# Revit family: RN 80033 Optipress-Aquaplus-Übergang
name_source: partatom
category: Rohrformteile
units: mm (PartAtom-declared; Revit-internal decimal feet)

## family parameters
Arbeitsebenenbasiert = Nein
Beim Laden mit Abzugskörper schneiden = Nein
Bemaßung runder Anschluss = Durchmesser verwenden
Gemeinsam genutzt = Nein
Immer vertikal = Ja
Teiletyp = Verbindung

## types (20) — shared parameters
1.010.00.2 Blattnummer der Richtlinie = 29
1.010.00.3 Ausgabedatum (Monat) der Richtlinie = 201308
1.010.00.4 Herstellername = R. Nussbaum AG
1.010.00.5 Revisionsdatum der Datei = 20190521
1.010.00.6 Webadresse des Herstellers = http://www.nussbaum.ch
1.100.00.4 Produktbezeichnung = Versorgung
1.110.00.2 Index = 4
1.110.00.4 Produktbezeichnung = Optipress
1.960/3L.00.8 Link (URL) = https://www.nussbaum.ch
29.700.00.4 Produktname = Optipress-Aquaplus-Übergang, mit Innengewinde
29.700.00.5 Produktkennung = 2
29.700.00.6 Querschnittsform = 1
29.700.00.7 Nennweitensystem = DN
29.700.00.8 Nenndrucksystem = PN
29.710.02.4 Nenndruck = 16
29.710.02.5 max. zul. Überdruck [hPa] = 1600
29.710.02.7 max. zul. Dauer-Betriebsdruck [hPa] = 1600
29.710.02.9 max. zul. Dauer-Betriebstemperatur [°C] = 95
Connector Visibility = Nein
EnclosingSpace Visibility = Nein

## per-type parameters (varying)
- 80033.22, Optipress-Aquaplus-Übergang, mit Innengewinde, DN=12x15, L=49, Rp=½: 1.800.00.3 TGA-Nummer=01900400000000000000000000000000000000000000000022000000000000000001; 1.810.00.3 Hersteller-Bestellnummer=80033.22; 1.810.00.4 DATANORM-Nummer=80033.22; 1.810.00.5 StLB-Nummer=267.132; 1.810.00.6 GTIN-Nummer=7612945051370; 29.710.02.10 Formstück-Gewicht [kg]=0.044; 29.710.02.3 Benennung=Optipress-Aquaplus-Übergang, mit Innengewinde, DN=12x15, L=49, Rp=½; CONNECTOR0_DIAMETER_dX_0r=12 mm  [stored 0.0393701 ft]; CONNECTOR0_dX_01=22 mm; CONNECTOR0_ref_dX=22 mm; CONNECTOR1_DIAMETER_dX_0r=15 mm  [stored 0.0492126 ft]; CONNECTOR1_dX_00=36 mm  [stored 0.11811 ft]; CONNECTOR1_dX_01=49 mm; CONNECTOR1_ref_dX=36 mm  [stored 0.11811 ft]; R. Nussbaum AG 80033.22 de Visibility=Ja; R. Nussbaum AG 80033.23 de Visibility=Nein; R. Nussbaum AG 80033.24 de Visibility=Nein; R. Nussbaum AG 80033.25 de Visibility=Nein; R. Nussbaum AG 80033.26 de Visibility=Nein; R. Nussbaum AG 80033.27 de Visibility=Nein; R. Nussbaum AG 80033.28 de Visibility=Nein; R. Nussbaum AG 80033.29 de Visibility=Nein; R. Nussbaum AG 80033.30 de Visibility=Nein; R. Nussbaum AG 80033.31 de Visibility=Nein; R. Nussbaum AG 80033.32 de Visibility=Nein; R. Nussbaum AG 80033.33 de Visibility=Nein; R. Nussbaum AG 80033.34 de Visibility=Nein; R. Nussbaum AG 80033.35 de Visibility=Nein; R. Nussbaum AG 80033.36 de Visibility=Nein; R. Nussbaum AG 80033.37 de Visibility=Nein; R. Nussbaum AG 80033.38 de Visibility=Nein; R. Nussbaum AG 80033.70 de Visibility=Nein; R. Nussbaum AG 80033.71 de Visibility=Nein; R. Nussbaum AG 80033.72 de Visibility=Nein
- 80033.23, Optipress-Aquaplus-Übergang, mit Innengewinde, DN=15, L=48, Rp=½: 1.800.00.3 TGA-Nummer=01900400000000000000000000000000000000000000000022000000000000000002; 1.810.00.3 Hersteller-Bestellnummer=80033.23; 1.810.00.4 DATANORM-Nummer=80033.23; 1.810.00.5 StLB-Nummer=267.133; 1.810.00.6 GTIN-Nummer=7612945051462; 29.710.02.10 Formstück-Gewicht [kg]=0.047; 29.710.02.3 Benennung=Optipress-Aquaplus-Übergang, mit Innengewinde, DN=15, L=48, Rp=½; CONNECTOR0_DIAMETER_dX_0r=15 mm  [stored 0.0492126 ft]; CONNECTOR0_dX_01=22 mm; CONNECTOR0_ref_dX=22 mm; CONNECTOR1_DIAMETER_dX_0r=15 mm  [stored 0.0492126 ft]; CONNECTOR1_dX_00=35 mm; CONNECTOR1_dX_01=48 mm; CONNECTOR1_ref_dX=35 mm; R. Nussbaum AG 80033.22 de Visibility=Nein; R. Nussbaum AG 80033.23 de Visibility=Ja; R. Nussbaum AG 80033.24 de Visibility=Nein; R. Nussbaum AG 80033.25 de Visibility=Nein; R. Nussbaum AG 80033.26 de Visibility=Nein; R. Nussbaum AG 80033.27 de Visibility=Nein; R. Nussbaum AG 80033.28 de Visibility=Nein; R. Nussbaum AG 80033.29 de Visibility=Nein; R. Nussbaum AG 80033.30 de Visibility=Nein; R. Nussbaum AG 80033.31 de Visibility=Nein; R. Nussbaum AG 80033.32 de Visibility=Nein; R. Nussbaum AG 80033.33 de Visibility=Nein; R. Nussbaum AG 80033.34 de Visibility=Nein; R. Nussbaum AG 80033.35 de Visibility=Nein; R. Nussbaum AG 80033.36 de Visibility=Nein; R. Nussbaum AG 80033.37 de Visibility=Nein; R. Nussbaum AG 80033.38 de Visibility=Nein; R. Nussbaum AG 80033.70 de Visibility=Nein; R. Nussbaum AG 80033.71 de Visibility=Nein; R. Nussbaum AG 80033.72 de Visibility=Nein
- 80033.24, Optipress-Aquaplus-Übergang, mit Innengewinde, DN=15, L=49, Rp=¾: 1.800.00.3 TGA-Nummer=01900400000000000000000000000000000000000000000022000000000000000003; 1.810.00.3 Hersteller-Bestellnummer=80033.24; 1.810.00.4 DATANORM-Nummer=80033.24; 1.810.00.6 GTIN-Nummer=7612945051479; 29.710.02.10 Formstück-Gewicht [kg]=0.063; 29.710.02.3 Benennung=Optipress-Aquaplus-Übergang, mit Innengewinde, DN=15, L=49, Rp=¾; CONNECTOR0_DIAMETER_dX_0r=15 mm  [stored 0.0492126 ft]; CONNECTOR0_dX_01=22 mm; CONNECTOR0_ref_dX=22 mm; CONNECTOR1_DIAMETER_dX_0r=20 mm; CONNECTOR1_dX_00=34 mm; CONNECTOR1_dX_01=49 mm; CONNECTOR1_ref_dX=34 mm; R. Nussbaum AG 80033.22 de Visibility=Nein; R. Nussbaum AG 80033.23 de Visibility=Nein; R. Nussbaum AG 80033.24 de Visibility=Ja; R. Nussbaum AG 80033.25 de Visibility=Nein; R. Nussbaum AG 80033.26 de Visibility=Nein; R. Nussbaum AG 80033.27 de Visibility=Nein; R. Nussbaum AG 80033.28 de Visibility=Nein; R. Nussbaum AG 80033.29 de Visibility=Nein; R. Nussbaum AG 80033.30 de Visibility=Nein; R. Nussbaum AG 80033.31 de Visibility=Nein; R. Nussbaum AG 80033.32 de Visibility=Nein; R. Nussbaum AG 80033.33 de Visibility=Nein; R. Nussbaum AG 80033.34 de Visibility=Nein; R. Nussbaum AG 80033.35 de Visibility=Nein; R. Nussbaum AG 80033.36 de Visibility=Nein; R. Nussbaum AG 80033.37 de Visibility=Nein; R. Nussbaum AG 80033.38 de Visibility=Nein; R. Nussbaum AG 80033.70 de Visibility=Nein; R. Nussbaum AG 80033.71 de Visibility=Nein; R. Nussbaum AG 80033.72 de Visibility=Nein
- 80033.25, Optipress-Aquaplus-Übergang, mit Innengewinde, DN=20, L=50, Rp=¾: 1.800.00.3 TGA-Nummer=01900400000000000000000000000000000000000000000022000000000000000004; 1.810.00.3 Hersteller-Bestellnummer=80033.25; 1.810.00.4 DATANORM-Nummer=80033.25; 1.810.00.5 StLB-Nummer=267.134; 1.810.00.6 GTIN-Nummer=7612945051493; 29.710.02.10 Formstück-Gewicht [kg]=0.069; 29.710.02.3 Benennung=Optipress-Aquaplus-Übergang, mit Innengewinde, DN=20, L=50, Rp=¾; CONNECTOR0_DIAMETER_dX_0r=20 mm; CONNECTOR0_dX_01=24 mm; CONNECTOR0_ref_dX=24 mm; CONNECTOR1_DIAMETER_dX_0r=20 mm; CONNECTOR1_dX_00=35 mm; CONNECTOR1_dX_01=50 mm; CONNECTOR1_ref_dX=35 mm; R. Nussbaum AG 80033.22 de Visibility=Nein; R. Nussbaum AG 80033.23 de Visibility=Nein; R. Nussbaum AG 80033.24 de Visibility=Nein; R. Nussbaum AG 80033.25 de Visibility=Ja; R. Nussbaum AG 80033.26 de Visibility=Nein; R. Nussbaum AG 80033.27 de Visibility=Nein; R. Nussbaum AG 80033.28 de Visibility=Nein; R. Nussbaum AG 80033.29 de Visibility=Nein; R. Nussbaum AG 80033.30 de Visibility=Nein; R. Nussbaum AG 80033.31 de Visibility=Nein; R. Nussbaum AG 80033.32 de Visibility=Nein; R. Nussbaum AG 80033.33 de Visibility=Nein; R. Nussbaum AG 80033.34 de Visibility=Nein; R. Nussbaum AG 80033.35 de Visibility=Nein; R. Nussbaum AG 80033.36 de Visibility=Nein; R. Nussbaum AG 80033.37 de Visibility=Nein; R. Nussbaum AG 80033.38 de Visibility=Nein; R. Nussbaum AG 80033.70 de Visibility=Nein; R. Nussbaum AG 80033.71 de Visibility=Nein; R. Nussbaum AG 80033.72 de Visibility=Nein
- 80033.26, Optipress-Aquaplus-Übergang, mit Innengewinde, DN=20x25, L=54, Rp=1: 1.800.00.3 TGA-Nummer=01900400000000000000000000000000000000000000000022000000000000000005; 1.810.00.3 Hersteller-Bestellnummer=80033.26; 1.810.00.4 DATANORM-Nummer=80033.26; 1.810.00.6 GTIN-Nummer=7612945051509; 29.710.02.10 Formstück-Gewicht [kg]=0.083; 29.710.02.3 Benennung=Optipress-Aquaplus-Übergang, mit Innengewinde, DN=20x25, L=54, Rp=1; CONNECTOR0_DIAMETER_dX_0r=20 mm; CONNECTOR0_dX_01=24 mm; CONNECTOR0_ref_dX=24 mm; CONNECTOR1_DIAMETER_dX_0r=25 mm  [stored 0.082021 ft]; CONNECTOR1_dX_00=36 mm  [stored 0.11811 ft]; CONNECTOR1_dX_01=53 mm; CONNECTOR1_ref_dX=36 mm  [stored 0.11811 ft]; R. Nussbaum AG 80033.22 de Visibility=Nein; R. Nussbaum AG 80033.23 de Visibility=Nein; R. Nussbaum AG 80033.24 de Visibility=Nein; R. Nussbaum AG 80033.25 de Visibility=Nein; R. Nussbaum AG 80033.26 de Visibility=Ja; R. Nussbaum AG 80033.27 de Visibility=Nein; R. Nussbaum AG 80033.28 de Visibility=Nein; R. Nussbaum AG 80033.29 de Visibility=Nein; R. Nussbaum AG 80033.30 de Visibility=Nein; R. Nussbaum AG 80033.31 de Visibility=Nein; R. Nussbaum AG 80033.32 de Visibility=Nein; R. Nussbaum AG 80033.33 de Visibility=Nein; R. Nussbaum AG 80033.34 de Visibility=Nein; R. Nussbaum AG 80033.35 de Visibility=Nein; R. Nussbaum AG 80033.36 de Visibility=Nein; R. Nussbaum AG 80033.37 de Visibility=Nein; R. Nussbaum AG 80033.38 de Visibility=Nein; R. Nussbaum AG 80033.70 de Visibility=Nein; R. Nussbaum AG 80033.71 de Visibility=Nein; R. Nussbaum AG 80033.72 de Visibility=Nein
- 80033.27, Optipress-Aquaplus-Übergang, mit Innengewinde, DN=25x20, L=51, Rp=¾: 1.800.00.3 TGA-Nummer=01900400000000000000000000000000000000000000000022000000000000000006; 1.810.00.3 Hersteller-Bestellnummer=80033.27; 1.810.00.4 DATANORM-Nummer=80033.27; 1.810.00.6 GTIN-Nummer=7612945051516; 29.710.02.10 Formstück-Gewicht [kg]=0.073; 29.710.02.3 Benennung=Optipress-Aquaplus-Übergang, mit Innengewinde, DN=25x20, L=51, Rp=¾; CONNECTOR0_DIAMETER_dX_0r=25 mm  [stored 0.082021 ft]; CONNECTOR0_dX_01=24 mm; CONNECTOR0_ref_dX=24 mm; CONNECTOR1_DIAMETER_dX_0r=20 mm; CONNECTOR1_dX_00=36 mm  [stored 0.11811 ft]; CONNECTOR1_dX_01=51 mm  [stored 0.167323 ft]; CONNECTOR1_ref_dX=36 mm  [stored 0.11811 ft]; R. Nussbaum AG 80033.22 de Visibility=Nein; R. Nussbaum AG 80033.23 de Visibility=Nein; R. Nussbaum AG 80033.24 de Visibility=Nein; R. Nussbaum AG 80033.25 de Visibility=Nein; R. Nussbaum AG 80033.26 de Visibility=Nein; R. Nussbaum AG 80033.27 de Visibility=Ja; R. Nussbaum AG 80033.28 de Visibility=Nein; R. Nussbaum AG 80033.29 de Visibility=Nein; R. Nussbaum AG 80033.30 de Visibility=Nein; R. Nussbaum AG 80033.31 de Visibility=Nein; R. Nussbaum AG 80033.32 de Visibility=Nein; R. Nussbaum AG 80033.33 de Visibility=Nein; R. Nussbaum AG 80033.34 de Visibility=Nein; R. Nussbaum AG 80033.35 de Visibility=Nein; R. Nussbaum AG 80033.36 de Visibility=Nein; R. Nussbaum AG 80033.37 de Visibility=Nein; R. Nussbaum AG 80033.38 de Visibility=Nein; R. Nussbaum AG 80033.70 de Visibility=Nein; R. Nussbaum AG 80033.71 de Visibility=Nein; R. Nussbaum AG 80033.72 de Visibility=Nein
- 80033.28, Optipress-Aquaplus-Übergang, mit Innengewinde, DN=25x32, L=57, Rp=1¼: 1.800.00.3 TGA-Nummer=01900400000000000000000000000000000000000000000022000000000000000007; 1.810.00.3 Hersteller-Bestellnummer=80033.28; 1.810.00.4 DATANORM-Nummer=80033.28; 1.810.00.6 GTIN-Nummer=7612945709813; 29.710.02.10 Formstück-Gewicht [kg]=0.136; 29.710.02.3 Benennung=Optipress-Aquaplus-Übergang, mit Innengewinde, DN=25x32, L=57, Rp=1¼; CONNECTOR0_DIAMETER_dX_0r=25 mm  [stored 0.082021 ft]; CONNECTOR0_dX_01=24 mm; CONNECTOR0_ref_dX=24 mm; CONNECTOR1_DIAMETER_dX_0r=32 mm; CONNECTOR1_dX_00=38 mm; CONNECTOR1_dX_01=57 mm; CONNECTOR1_ref_dX=38 mm; R. Nussbaum AG 80033.22 de Visibility=Nein; R. Nussbaum AG 80033.23 de Visibility=Nein; R. Nussbaum AG 80033.24 de Visibility=Nein; R. Nussbaum AG 80033.25 de Visibility=Nein; R. Nussbaum AG 80033.26 de Visibility=Nein; R. Nussbaum AG 80033.27 de Visibility=Nein; R. Nussbaum AG 80033.28 de Visibility=Ja; R. Nussbaum AG 80033.29 de Visibility=Nein; R. Nussbaum AG 80033.30 de Visibility=Nein; R. Nussbaum AG 80033.31 de Visibility=Nein; R. Nussbaum AG 80033.32 de Visibility=Nein; R. Nussbaum AG 80033.33 de Visibility=Nein; R. Nussbaum AG 80033.34 de Visibility=Nein; R. Nussbaum AG 80033.35 de Visibility=Nein; R. Nussbaum AG 80033.36 de Visibility=Nein; R. Nussbaum AG 80033.37 de Visibility=Nein; R. Nussbaum AG 80033.38 de Visibility=Nein; R. Nussbaum AG 80033.70 de Visibility=Nein; R. Nussbaum AG 80033.71 de Visibility=Nein; R. Nussbaum AG 80033.72 de Visibility=Nein
- 80033.29, Optipress-Aquaplus-Übergang, mit Innengewinde, DN=25, L=54, Rp=1: 1.800.00.3 TGA-Nummer=01900400000000000000000000000000000000000000000022000000000000000008; 1.810.00.3 Hersteller-Bestellnummer=80033.29; 1.810.00.4 DATANORM-Nummer=80033.29; 1.810.00.5 StLB-Nummer=267.135; 1.810.00.6 GTIN-Nummer=7612945051523; 29.710.02.10 Formstück-Gewicht [kg]=0.092; 29.710.02.3 Benennung=Optipress-Aquaplus-Übergang, mit Innengewinde, DN=25, L=54, Rp=1; CONNECTOR0_DIAMETER_dX_0r=25 mm  [stored 0.082021 ft]; CONNECTOR0_dX_01=24 mm; CONNECTOR0_ref_dX=24 mm; CONNECTOR1_DIAMETER_dX_0r=25 mm  [stored 0.082021 ft]; CONNECTOR1_dX_00=37 mm  [stored 0.121391 ft]; CONNECTOR1_dX_01=54 mm; CONNECTOR1_ref_dX=37 mm  [stored 0.121391 ft]; R. Nussbaum AG 80033.22 de Visibility=Nein; R. Nussbaum AG 80033.23 de Visibility=Nein; R. Nussbaum AG 80033.24 de Visibility=Nein; R. Nussbaum AG 80033.25 de Visibility=Nein; R. Nussbaum AG 80033.26 de Visibility=Nein; R. Nussbaum AG 80033.27 de Visibility=Nein; R. Nussbaum AG 80033.28 de Visibility=Nein; R. Nussbaum AG 80033.29 de Visibility=Ja; R. Nussbaum AG 80033.30 de Visibility=Nein; R. Nussbaum AG 80033.31 de Visibility=Nein; R. Nussbaum AG 80033.32 de Visibility=Nein; R. Nussbaum AG 80033.33 de Visibility=Nein; R. Nussbaum AG 80033.34 de Visibility=Nein; R. Nussbaum AG 80033.35 de Visibility=Nein; R. Nussbaum AG 80033.36 de Visibility=Nein; R. Nussbaum AG 80033.37 de Visibility=Nein; R. Nussbaum AG 80033.38 de Visibility=Nein; R. Nussbaum AG 80033.70 de Visibility=Nein; R. Nussbaum AG 80033.71 de Visibility=Nein; R. Nussbaum AG 80033.72 de Visibility=Nein
- 80033.31, Optipress-Aquaplus-Übergang, mit Innengewinde, DN=32, L=60, Rp=1¼: 1.800.00.3 TGA-Nummer=01900400000000000000000000000000000000000000000022000000000000000009; 1.810.00.3 Hersteller-Bestellnummer=80033.31; 1.810.00.4 DATANORM-Nummer=80033.31; 1.810.00.5 StLB-Nummer=267.136; 1.810.00.6 GTIN-Nummer=7612945051530; 29.710.02.10 Formstück-Gewicht [kg]=0.143; 29.710.02.3 Benennung=Optipress-Aquaplus-Übergang, mit Innengewinde, DN=32, L=60, Rp=1¼; CONNECTOR0_DIAMETER_dX_0r=32 mm; CONNECTOR0_dX_01=26 mm; CONNECTOR0_ref_dX=26 mm; CONNECTOR1_DIAMETER_dX_0r=32 mm; CONNECTOR1_dX_00=41 mm; CONNECTOR1_dX_01=60 mm; CONNECTOR1_ref_dX=41 mm; R. Nussbaum AG 80033.22 de Visibility=Nein; R. Nussbaum AG 80033.23 de Visibility=Nein; R. Nussbaum AG 80033.24 de Visibility=Nein; R. Nussbaum AG 80033.25 de Visibility=Nein; R. Nussbaum AG 80033.26 de Visibility=Nein; R. Nussbaum AG 80033.27 de Visibility=Nein; R. Nussbaum AG 80033.28 de Visibility=Nein; R. Nussbaum AG 80033.29 de Visibility=Nein; R. Nussbaum AG 80033.30 de Visibility=Nein; R. Nussbaum AG 80033.31 de Visibility=Ja; R. Nussbaum AG 80033.32 de Visibility=Nein; R. Nussbaum AG 80033.33 de Visibility=Nein; R. Nussbaum AG 80033.34 de Visibility=Nein; R. Nussbaum AG 80033.35 de Visibility=Nein; R. Nussbaum AG 80033.36 de Visibility=Nein; R. Nussbaum AG 80033.37 de Visibility=Nein; R. Nussbaum AG 80033.38 de Visibility=Nein; R. Nussbaum AG 80033.70 de Visibility=Nein; R. Nussbaum AG 80033.71 de Visibility=Nein; R. Nussbaum AG 80033.72 de Visibility=Nein
- 80033.32, Optipress-Aquaplus-Übergang, mit Innengewinde, DN=32x40, L=60, Rp=1½: 1.800.00.3 TGA-Nummer=01900400000000000000000000000000000000000000000022000000000000000010; 1.810.00.3 Hersteller-Bestellnummer=80033.32; 1.810.00.4 DATANORM-Nummer=80033.32; 1.810.00.6 GTIN-Nummer=7612945709837; 29.710.02.10 Formstück-Gewicht [kg]=0.215; 29.710.02.3 Benennung=Optipress-Aquaplus-Übergang, mit Innengewinde, DN=32x40, L=60, Rp=1½; CONNECTOR0_DIAMETER_dX_0r=32 mm; CONNECTOR0_dX_01=26 mm; CONNECTOR0_ref_dX=26 mm; CONNECTOR1_DIAMETER_dX_0r=40 mm; CONNECTOR1_dX_00=41 mm; CONNECTOR1_dX_01=60 mm; CONNECTOR1_ref_dX=41 mm; R. Nussbaum AG 80033.22 de Visibility=Nein; R. Nussbaum AG 80033.23 de Visibility=Nein; R. Nussbaum AG 80033.24 de Visibility=Nein; R. Nussbaum AG 80033.25 de Visibility=Nein; R. Nussbaum AG 80033.26 de Visibility=Nein; R. Nussbaum AG 80033.27 de Visibility=Nein; R. Nussbaum AG 80033.28 de Visibility=Nein; R. Nussbaum AG 80033.29 de Visibility=Nein; R. Nussbaum AG 80033.30 de Visibility=Nein; R. Nussbaum AG 80033.31 de Visibility=Nein; R. Nussbaum AG 80033.32 de Visibility=Ja; R. Nussbaum AG 80033.33 de Visibility=Nein; R. Nussbaum AG 80033.34 de Visibility=Nein; R. Nussbaum AG 80033.35 de Visibility=Nein; R. Nussbaum AG 80033.36 de Visibility=Nein; R. Nussbaum AG 80033.37 de Visibility=Nein; R. Nussbaum AG 80033.38 de Visibility=Nein; R. Nussbaum AG 80033.70 de Visibility=Nein; R. Nussbaum AG 80033.71 de Visibility=Nein; R. Nussbaum AG 80033.72 de Visibility=Nein
- 80033.33, Optipress-Aquaplus-Übergang, mit Innengewinde, DN=40, L=72, Rp=1½: 1.800.00.3 TGA-Nummer=01900400000000000000000000000000000000000000000022000000000000000011; 1.810.00.3 Hersteller-Bestellnummer=80033.33; 1.810.00.4 DATANORM-Nummer=80033.33; 1.810.00.5 StLB-Nummer=267.137; 1.810.00.6 GTIN-Nummer=7612945051547; 29.710.02.10 Formstück-Gewicht [kg]=0.262; 29.710.02.3 Benennung=Optipress-Aquaplus-Übergang, mit Innengewinde, DN=40, L=72, Rp=1½; CONNECTOR0_DIAMETER_dX_0r=40 mm; CONNECTOR0_dX_01=36 mm  [stored 0.11811 ft]; CONNECTOR0_ref_dX=36 mm  [stored 0.11811 ft]; CONNECTOR1_DIAMETER_dX_0r=40 mm; CONNECTOR1_dX_00=53 mm; CONNECTOR1_dX_01=72 mm; CONNECTOR1_ref_dX=53 mm; R. Nussbaum AG 80033.22 de Visibility=Nein; R. Nussbaum AG 80033.23 de Visibility=Nein; R. Nussbaum AG 80033.24 de Visibility=Nein; R. Nussbaum AG 80033.25 de Visibility=Nein; R. Nussbaum AG 80033.26 de Visibility=Nein; R. Nussbaum AG 80033.27 de Visibility=Nein; R. Nussbaum AG 80033.28 de Visibility=Nein; R. Nussbaum AG 80033.29 de Visibility=Nein; R. Nussbaum AG 80033.30 de Visibility=Nein; R. Nussbaum AG 80033.31 de Visibility=Nein; R. Nussbaum AG 80033.32 de Visibility=Nein; R. Nussbaum AG 80033.33 de Visibility=Ja; R. Nussbaum AG 80033.34 de Visibility=Nein; R. Nussbaum AG 80033.35 de Visibility=Nein; R. Nussbaum AG 80033.36 de Visibility=Nein; R. Nussbaum AG 80033.37 de Visibility=Nein; R. Nussbaum AG 80033.38 de Visibility=Nein; R. Nussbaum AG 80033.70 de Visibility=Nein; R. Nussbaum AG 80033.71 de Visibility=Nein; R. Nussbaum AG 80033.72 de Visibility=Nein
- 80033.34, Optipress-Aquaplus-Übergang, mit Innengewinde, DN=40x32, L=71, Rp=1¼: 1.800.00.3 TGA-Nummer=01900400000000000000000000000000000000000000000022000000000000000012; 1.810.00.3 Hersteller-Bestellnummer=80033.34; 1.810.00.4 DATANORM-Nummer=80033.34; 1.810.00.6 GTIN-Nummer=7612945709844; 29.710.02.10 Formstück-Gewicht [kg]=0.191; 29.710.02.3 Benennung=Optipress-Aquaplus-Übergang, mit Innengewinde, DN=40x32, L=71, Rp=1¼; CONNECTOR0_DIAMETER_dX_0r=40 mm; CONNECTOR0_dX_01=36 mm  [stored 0.11811 ft]; CONNECTOR0_ref_dX=36 mm  [stored 0.11811 ft]; CONNECTOR1_DIAMETER_dX_0r=32 mm; CONNECTOR1_dX_00=52 mm; CONNECTOR1_dX_01=71 mm; CONNECTOR1_ref_dX=52 mm; R. Nussbaum AG 80033.22 de Visibility=Nein; R. Nussbaum AG 80033.23 de Visibility=Nein; R. Nussbaum AG 80033.24 de Visibility=Nein; R. Nussbaum AG 80033.25 de Visibility=Nein; R. Nussbaum AG 80033.26 de Visibility=Nein; R. Nussbaum AG 80033.27 de Visibility=Nein; R. Nussbaum AG 80033.28 de Visibility=Nein; R. Nussbaum AG 80033.29 de Visibility=Nein; R. Nussbaum AG 80033.30 de Visibility=Nein; R. Nussbaum AG 80033.31 de Visibility=Nein; R. Nussbaum AG 80033.32 de Visibility=Nein; R. Nussbaum AG 80033.33 de Visibility=Nein; R. Nussbaum AG 80033.34 de Visibility=Ja; R. Nussbaum AG 80033.35 de Visibility=Nein; R. Nussbaum AG 80033.36 de Visibility=Nein; R. Nussbaum AG 80033.37 de Visibility=Nein; R. Nussbaum AG 80033.38 de Visibility=Nein; R. Nussbaum AG 80033.70 de Visibility=Nein; R. Nussbaum AG 80033.71 de Visibility=Nein; R. Nussbaum AG 80033.72 de Visibility=Nein
- 80033.35, Optipress-Aquaplus-Übergang, mit Innengewinde, DN=50, L=83, Rp=2: 1.800.00.3 TGA-Nummer=01900400000000000000000000000000000000000000000022000000000000000013; 1.810.00.3 Hersteller-Bestellnummer=80033.35; 1.810.00.4 DATANORM-Nummer=80033.35; 1.810.00.5 StLB-Nummer=267.138; 1.810.00.6 GTIN-Nummer=7612945051554; 29.710.02.10 Formstück-Gewicht [kg]=0.333; 29.710.02.3 Benennung=Optipress-Aquaplus-Übergang, mit Innengewinde, DN=50, L=83, Rp=2; CONNECTOR0_DIAMETER_dX_0r=50 mm; CONNECTOR0_dX_01=40 mm; CONNECTOR0_ref_dX=40 mm; CONNECTOR1_DIAMETER_dX_0r=50 mm; CONNECTOR1_dX_00=59 mm; CONNECTOR1_dX_01=83 mm; CONNECTOR1_ref_dX=59 mm; R. Nussbaum AG 80033.22 de Visibility=Nein; R. Nussbaum AG 80033.23 de Visibility=Nein; R. Nussbaum AG 80033.24 de Visibility=Nein; R. Nussbaum AG 80033.25 de Visibility=Nein; R. Nussbaum AG 80033.26 de Visibility=Nein; R. Nussbaum AG 80033.27 de Visibility=Nein; R. Nussbaum AG 80033.28 de Visibility=Nein; R. Nussbaum AG 80033.29 de Visibility=Nein; R. Nussbaum AG 80033.30 de Visibility=Nein; R. Nussbaum AG 80033.31 de Visibility=Nein; R. Nussbaum AG 80033.32 de Visibility=Nein; R. Nussbaum AG 80033.33 de Visibility=Nein; R. Nussbaum AG 80033.34 de Visibility=Nein; R. Nussbaum AG 80033.35 de Visibility=Ja; R. Nussbaum AG 80033.36 de Visibility=Nein; R. Nussbaum AG 80033.37 de Visibility=Nein; R. Nussbaum AG 80033.38 de Visibility=Nein; R. Nussbaum AG 80033.70 de Visibility=Nein; R. Nussbaum AG 80033.71 de Visibility=Nein; R. Nussbaum AG 80033.72 de Visibility=Nein
- 80033.36, Optipress-Aquaplus-Übergang, mit Innengewinde, DN=15x20, L=50, Rp=¾: 1.800.00.3 TGA-Nummer=01900400000000000000000000000000000000000000000022000000000000000014; 1.810.00.3 Hersteller-Bestellnummer=80033.36; 1.810.00.4 DATANORM-Nummer=80033.36; 1.810.00.6 GTIN-Nummer=7612945051455; 29.710.02.10 Formstück-Gewicht [kg]=0.059; 29.710.02.3 Benennung=Optipress-Aquaplus-Übergang, mit Innengewinde, DN=15x20, L=50, Rp=¾; CONNECTOR0_DIAMETER_dX_0r=15 mm  [stored 0.0492126 ft]; CONNECTOR0_dX_01=22 mm; CONNECTOR0_ref_dX=22 mm; CONNECTOR1_DIAMETER_dX_0r=20 mm; CONNECTOR1_dX_00=35 mm; CONNECTOR1_dX_01=50 mm; CONNECTOR1_ref_dX=35 mm; R. Nussbaum AG 80033.22 de Visibility=Nein; R. Nussbaum AG 80033.23 de Visibility=Nein; R. Nussbaum AG 80033.24 de Visibility=Nein; R. Nussbaum AG 80033.25 de Visibility=Nein; R. Nussbaum AG 80033.26 de Visibility=Nein; R. Nussbaum AG 80033.27 de Visibility=Nein; R. Nussbaum AG 80033.28 de Visibility=Nein; R. Nussbaum AG 80033.29 de Visibility=Nein; R. Nussbaum AG 80033.30 de Visibility=Nein; R. Nussbaum AG 80033.31 de Visibility=Nein; R. Nussbaum AG 80033.32 de Visibility=Nein; R. Nussbaum AG 80033.33 de Visibility=Nein; R. Nussbaum AG 80033.34 de Visibility=Nein; R. Nussbaum AG 80033.35 de Visibility=Nein; R. Nussbaum AG 80033.36 de Visibility=Ja; R. Nussbaum AG 80033.37 de Visibility=Nein; R. Nussbaum AG 80033.38 de Visibility=Nein; R. Nussbaum AG 80033.70 de Visibility=Nein; R. Nussbaum AG 80033.71 de Visibility=Nein; R. Nussbaum AG 80033.72 de Visibility=Nein
- 80033.37, Optipress-Aquaplus-Übergang, mit Innengewinde, DN=20x15, L=49, Rp=½: 1.800.00.3 TGA-Nummer=01900400000000000000000000000000000000000000000022000000000000000015; 1.810.00.3 Hersteller-Bestellnummer=80033.37; 1.810.00.4 DATANORM-Nummer=80033.37; 1.810.00.6 GTIN-Nummer=7612945051486; 29.710.02.10 Formstück-Gewicht [kg]=0.053; 29.710.02.3 Benennung=Optipress-Aquaplus-Übergang, mit Innengewinde, DN=20x15, L=49, Rp=½; CONNECTOR0_DIAMETER_dX_0r=20 mm; CONNECTOR0_dX_01=24 mm; CONNECTOR0_ref_dX=24 mm; CONNECTOR1_DIAMETER_dX_0r=15 mm  [stored 0.0492126 ft]; CONNECTOR1_dX_00=36 mm  [stored 0.11811 ft]; CONNECTOR1_dX_01=49 mm; CONNECTOR1_ref_dX=36 mm  [stored 0.11811 ft]; R. Nussbaum AG 80033.22 de Visibility=Nein; R. Nussbaum AG 80033.23 de Visibility=Nein; R. Nussbaum AG 80033.24 de Visibility=Nein; R. Nussbaum AG 80033.25 de Visibility=Nein; R. Nussbaum AG 80033.26 de Visibility=Nein; R. Nussbaum AG 80033.27 de Visibility=Nein; R. Nussbaum AG 80033.28 de Visibility=Nein; R. Nussbaum AG 80033.29 de Visibility=Nein; R. Nussbaum AG 80033.30 de Visibility=Nein; R. Nussbaum AG 80033.31 de Visibility=Nein; R. Nussbaum AG 80033.32 de Visibility=Nein; R. Nussbaum AG 80033.33 de Visibility=Nein; R. Nussbaum AG 80033.34 de Visibility=Nein; R. Nussbaum AG 80033.35 de Visibility=Nein; R. Nussbaum AG 80033.36 de Visibility=Nein; R. Nussbaum AG 80033.37 de Visibility=Ja; R. Nussbaum AG 80033.38 de Visibility=Nein; R. Nussbaum AG 80033.70 de Visibility=Nein; R. Nussbaum AG 80033.71 de Visibility=Nein; R. Nussbaum AG 80033.72 de Visibility=Nein
- 80033.38, Optipress-Aquaplus-Übergang, mit Innengewinde, DN=50x40, L=75, Rp=1½: 1.800.00.3 TGA-Nummer=01900400000000000000000000000000000000000000000022000000000000000016; 1.810.00.3 Hersteller-Bestellnummer=80033.38; 1.810.00.4 DATANORM-Nummer=80033.38; 1.810.00.6 GTIN-Nummer=7612945709851; 29.710.02.10 Formstück-Gewicht [kg]=0.274; 29.710.02.3 Benennung=Optipress-Aquaplus-Übergang, mit Innengewinde, DN=50x40, L=75, Rp=1½; CONNECTOR0_DIAMETER_dX_0r=50 mm; CONNECTOR0_dX_01=40 mm; CONNECTOR0_ref_dX=40 mm; CONNECTOR1_DIAMETER_dX_0r=40 mm; CONNECTOR1_dX_00=56 mm; CONNECTOR1_dX_01=75 mm; CONNECTOR1_ref_dX=56 mm; R. Nussbaum AG 80033.22 de Visibility=Nein; R. Nussbaum AG 80033.23 de Visibility=Nein; R. Nussbaum AG 80033.24 de Visibility=Nein; R. Nussbaum AG 80033.25 de Visibility=Nein; R. Nussbaum AG 80033.26 de Visibility=Nein; R. Nussbaum AG 80033.27 de Visibility=Nein; R. Nussbaum AG 80033.28 de Visibility=Nein; R. Nussbaum AG 80033.29 de Visibility=Nein; R. Nussbaum AG 80033.30 de Visibility=Nein; R. Nussbaum AG 80033.31 de Visibility=Nein; R. Nussbaum AG 80033.32 de Visibility=Nein; R. Nussbaum AG 80033.33 de Visibility=Nein; R. Nussbaum AG 80033.34 de Visibility=Nein; R. Nussbaum AG 80033.35 de Visibility=Nein; R. Nussbaum AG 80033.36 de Visibility=Nein; R. Nussbaum AG 80033.37 de Visibility=Nein; R. Nussbaum AG 80033.38 de Visibility=Ja; R. Nussbaum AG 80033.70 de Visibility=Nein; R. Nussbaum AG 80033.71 de Visibility=Nein; R. Nussbaum AG 80033.72 de Visibility=Nein
- 80033.71, Optipress-Aquaplus-Übergang, mit Innengewinde, DN=65, L=104, Rp=2½: 1.800.00.3 TGA-Nummer=01900400000000000000000000000000000000000000000022000000000000000017; 1.810.00.3 Hersteller-Bestellnummer=80033.71; 1.810.00.4 DATANORM-Nummer=80033.71; 1.810.00.5 StLB-Nummer=267.141; 1.810.00.6 GTIN-Nummer=7612945682536; 29.710.02.10 Formstück-Gewicht [kg]=0.669; 29.710.02.3 Benennung=Optipress-Aquaplus-Übergang, mit Innengewinde, DN=65, L=104, Rp=2½; CONNECTOR0_DIAMETER_dX_0r=65 mm; CONNECTOR0_dX_01=50 mm; CONNECTOR0_ref_dX=50 mm; CONNECTOR1_DIAMETER_dX_0r=65 mm; CONNECTOR1_dX_00=77 mm; CONNECTOR1_dX_01=104 mm; CONNECTOR1_ref_dX=77 mm; R. Nussbaum AG 80033.22 de Visibility=Nein; R. Nussbaum AG 80033.23 de Visibility=Nein; R. Nussbaum AG 80033.24 de Visibility=Nein; R. Nussbaum AG 80033.25 de Visibility=Nein; R. Nussbaum AG 80033.26 de Visibility=Nein; R. Nussbaum AG 80033.27 de Visibility=Nein; R. Nussbaum AG 80033.28 de Visibility=Nein; R. Nussbaum AG 80033.29 de Visibility=Nein; R. Nussbaum AG 80033.30 de Visibility=Nein; R. Nussbaum AG 80033.31 de Visibility=Nein; R. Nussbaum AG 80033.32 de Visibility=Nein; R. Nussbaum AG 80033.33 de Visibility=Nein; R. Nussbaum AG 80033.34 de Visibility=Nein; R. Nussbaum AG 80033.35 de Visibility=Nein; R. Nussbaum AG 80033.36 de Visibility=Nein; R. Nussbaum AG 80033.37 de Visibility=Nein; R. Nussbaum AG 80033.38 de Visibility=Nein; R. Nussbaum AG 80033.70 de Visibility=Nein; R. Nussbaum AG 80033.71 de Visibility=Ja; R. Nussbaum AG 80033.72 de Visibility=Nein
- 80033.72, Optipress-Aquaplus-Übergang, mit Innengewinde, DN=80, L=114, Rp=3: 1.800.00.3 TGA-Nummer=01900400000000000000000000000000000000000000000022000000000000000018; 1.810.00.3 Hersteller-Bestellnummer=80033.72; 1.810.00.4 DATANORM-Nummer=80033.72; 1.810.00.5 StLB-Nummer=267.142; 1.810.00.6 GTIN-Nummer=7612945682543; 29.710.02.10 Formstück-Gewicht [kg]=1.178; 29.710.02.3 Benennung=Optipress-Aquaplus-Übergang, mit Innengewinde, DN=80, L=114, Rp=3; CONNECTOR0_DIAMETER_dX_0r=80 mm; CONNECTOR0_dX_01=50 mm; CONNECTOR0_ref_dX=50 mm; CONNECTOR1_DIAMETER_dX_0r=80 mm; CONNECTOR1_dX_00=84 mm; CONNECTOR1_dX_01=114 mm; CONNECTOR1_ref_dX=84 mm; R. Nussbaum AG 80033.22 de Visibility=Nein; R. Nussbaum AG 80033.23 de Visibility=Nein; R. Nussbaum AG 80033.24 de Visibility=Nein; R. Nussbaum AG 80033.25 de Visibility=Nein; R. Nussbaum AG 80033.26 de Visibility=Nein; R. Nussbaum AG 80033.27 de Visibility=Nein; R. Nussbaum AG 80033.28 de Visibility=Nein; R. Nussbaum AG 80033.29 de Visibility=Nein; R. Nussbaum AG 80033.30 de Visibility=Nein; R. Nussbaum AG 80033.31 de Visibility=Nein; R. Nussbaum AG 80033.32 de Visibility=Nein; R. Nussbaum AG 80033.33 de Visibility=Nein; R. Nussbaum AG 80033.34 de Visibility=Nein; R. Nussbaum AG 80033.35 de Visibility=Nein; R. Nussbaum AG 80033.36 de Visibility=Nein; R. Nussbaum AG 80033.37 de Visibility=Nein; R. Nussbaum AG 80033.38 de Visibility=Nein; R. Nussbaum AG 80033.70 de Visibility=Nein; R. Nussbaum AG 80033.71 de Visibility=Nein; R. Nussbaum AG 80033.72 de Visibility=Ja
- 80033.30, Optipress-Aquaplus-Übergang, mit Innengewinde, DN=32x25, L=56, Rp=1: 1.800.00.3 TGA-Nummer=01900400000000000000000000000000000000000000000022000000000000000038; 1.810.00.3 Hersteller-Bestellnummer=80033.30; 1.810.00.4 DATANORM-Nummer=80033.30; 1.810.00.6 GTIN-Nummer=7612945709820; 29.710.02.10 Formstück-Gewicht [kg]=0.099; 29.710.02.3 Benennung=Optipress-Aquaplus-Übergang, mit Innengewinde, DN=32x25, L=56, Rp=1; CONNECTOR0_DIAMETER_dX_0r=32 mm; CONNECTOR0_dX_01=26 mm; CONNECTOR0_ref_dX=26 mm; CONNECTOR1_DIAMETER_dX_0r=25 mm  [stored 0.082021 ft]; CONNECTOR1_dX_00=39 mm; CONNECTOR1_dX_01=56 mm; CONNECTOR1_ref_dX=39 mm; R. Nussbaum AG 80033.22 de Visibility=Nein; R. Nussbaum AG 80033.23 de Visibility=Nein; R. Nussbaum AG 80033.24 de Visibility=Nein; R. Nussbaum AG 80033.25 de Visibility=Nein; R. Nussbaum AG 80033.26 de Visibility=Nein; R. Nussbaum AG 80033.27 de Visibility=Nein; R. Nussbaum AG 80033.28 de Visibility=Nein; R. Nussbaum AG 80033.29 de Visibility=Nein; R. Nussbaum AG 80033.30 de Visibility=Ja; R. Nussbaum AG 80033.31 de Visibility=Nein; R. Nussbaum AG 80033.32 de Visibility=Nein; R. Nussbaum AG 80033.33 de Visibility=Nein; R. Nussbaum AG 80033.34 de Visibility=Nein; R. Nussbaum AG 80033.35 de Visibility=Nein; R. Nussbaum AG 80033.36 de Visibility=Nein; R. Nussbaum AG 80033.37 de Visibility=Nein; R. Nussbaum AG 80033.38 de Visibility=Nein; R. Nussbaum AG 80033.70 de Visibility=Nein; R. Nussbaum AG 80033.71 de Visibility=Nein; R. Nussbaum AG 80033.72 de Visibility=Nein
- 80033.70, Optipress-Aquaplus-Übergang, mit Innengewinde, DN=60x65, L=98, Rp=2½: 1.800.00.3 TGA-Nummer=01900400000000000000000000000000000000000000000022000000000000000039; 1.810.00.3 Hersteller-Bestellnummer=80033.70; 1.810.00.4 DATANORM-Nummer=80033.70; 1.810.00.5 StLB-Nummer=267.144; 1.810.00.6 GTIN-Nummer=7612945682529; 29.710.02.10 Formstück-Gewicht [kg]=0.643; 29.710.02.3 Benennung=Optipress-Aquaplus-Übergang, mit Innengewinde, DN=60x65, L=98, Rp=2½; CONNECTOR0_DIAMETER_dX_0r=60 mm; CONNECTOR0_dX_01=43 mm  [stored 0.141076 ft]; CONNECTOR0_ref_dX=43 mm  [stored 0.141076 ft]; CONNECTOR1_DIAMETER_dX_0r=50 mm; CONNECTOR1_dX_00=99 mm; CONNECTOR1_dX_01=123 mm; CONNECTOR1_ref_dX=123 mm; R. Nussbaum AG 80033.22 de Visibility=Nein; R. Nussbaum AG 80033.23 de Visibility=Nein; R. Nussbaum AG 80033.24 de Visibility=Nein; R. Nussbaum AG 80033.25 de Visibility=Nein; R. Nussbaum AG 80033.26 de Visibility=Nein; R. Nussbaum AG 80033.27 de Visibility=Nein; R. Nussbaum AG 80033.28 de Visibility=Nein; R. Nussbaum AG 80033.29 de Visibility=Nein; R. Nussbaum AG 80033.30 de Visibility=Nein; R. Nussbaum AG 80033.31 de Visibility=Nein; R. Nussbaum AG 80033.32 de Visibility=Nein; R. Nussbaum AG 80033.33 de Visibility=Nein; R. Nussbaum AG 80033.34 de Visibility=Nein; R. Nussbaum AG 80033.35 de Visibility=Nein; R. Nussbaum AG 80033.36 de Visibility=Nein; R. Nussbaum AG 80033.37 de Visibility=Nein; R. Nussbaum AG 80033.38 de Visibility=Nein; R. Nussbaum AG 80033.70 de Visibility=Ja; R. Nussbaum AG 80033.71 de Visibility=Nein; R. Nussbaum AG 80033.72 de Visibility=Nein

note: column(s) folded — value = type name in every type: 1.800.00.4 Kommentarfeld

note: [stored X ft] marks values corroborated as IEEE doubles in the binary element streams (Revit-internal decimal feet)

## geometry (parser evidence)
native form markers: Sweep x3
no freeform markers — native parametric forms only
